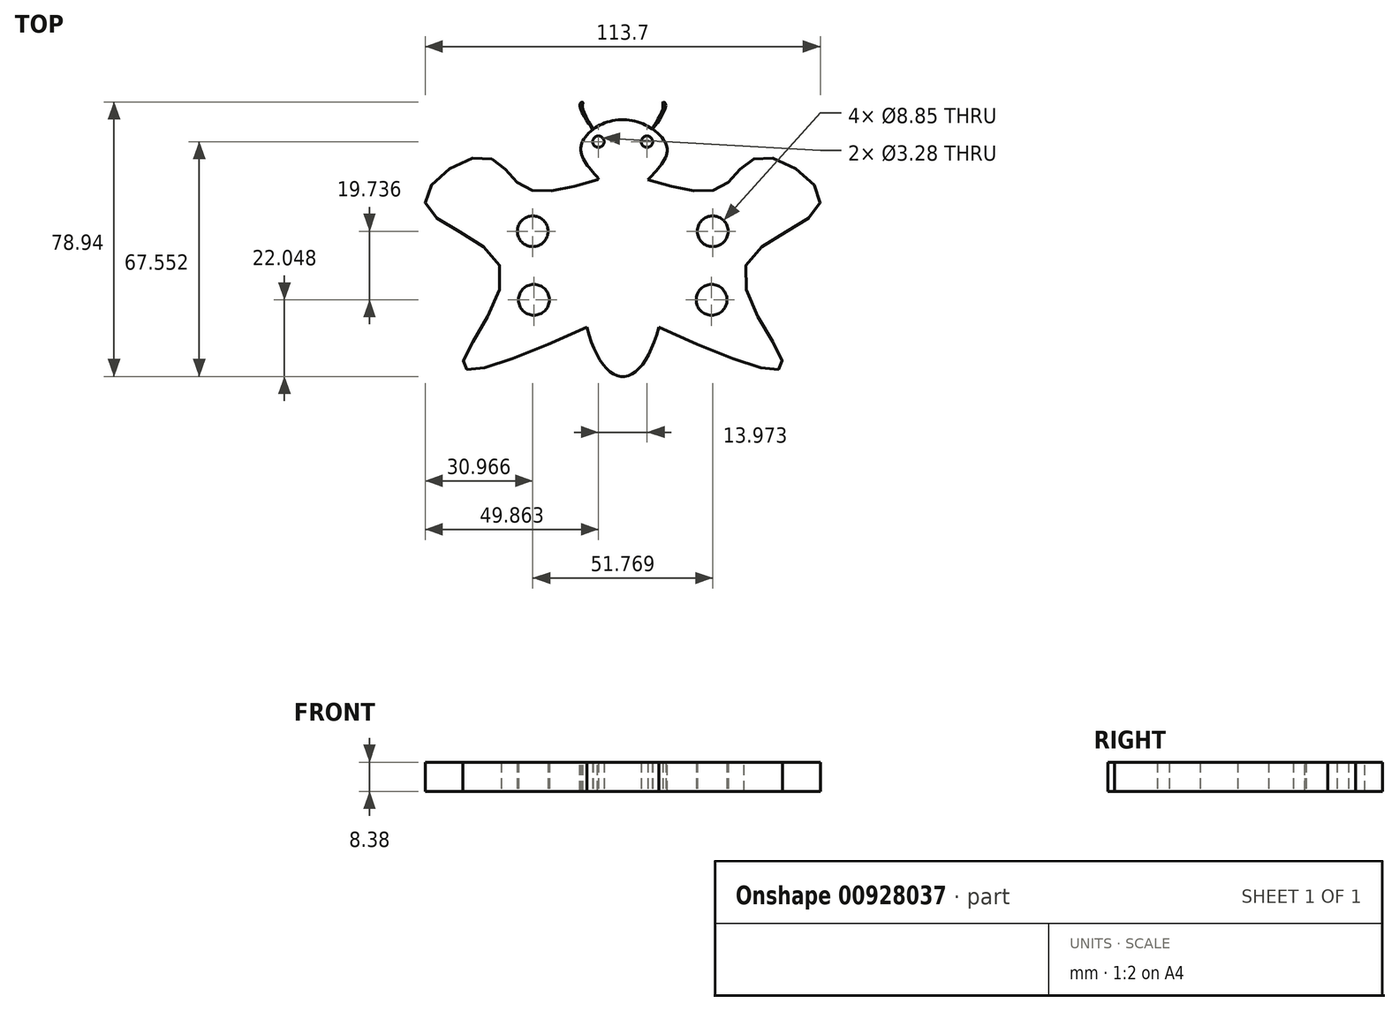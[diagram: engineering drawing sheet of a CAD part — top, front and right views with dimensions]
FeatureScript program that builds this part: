
annotation { "Feature Type Name" : "Feature", "Feature Type Description" : "" }
export const myFeature = defineFeature(function(context is Context, id is Id, definition is map)
    precondition{}
    {
        {
            var Q0;
            Q0=qCreatedBy(makeId("Top.planeOp"),FACE);
            var sketch = newSketch(context, id + "F0", { "sketchPlane" : qUnion([Q0])});
            skEllipse(sketch, "E0", {"center": v(0, 0) * mm, "majorRadius": 31.25 * mm, "minorRadius": 12.36 * mm, "majorAxis": v(0, -1)});
            skFitSpline(sketch, "E1", {"points": [v(-6.99, 25.78) * mm, v(-11.98, 35.24) * mm, v(0, 42.68) * mm, v(12.68, 34.77) * mm, v(7.23, 25.35) * mm], "startDerivative": vector(-36.9, 40.54) * mm, "endDerivative": vector(-38.54, -39.6) * mm});
            skCircle(sketch, "E2", {"center": v(-6.99, 36.3) * mm, "radius": 1.64 * mm});
            skCircle(sketch, "E3.MirrorC", {"center": v(6.99, 36.3) * mm, "radius": 1.64 * mm});
            skFitSpline(sketch, "E4", {"points": [v(7.23, 25.35) * mm, v(28.57, 23.33) * mm, v(39.9, 31.9) * mm, v(56.78, 18.63) * mm, v(35.2, 0) * mm, v(46, -27.84) * mm, v(10.34, -17.1) * mm], "startDerivative": vector(158.4, -47.63) * mm, "endDerivative": vector(-259.87, 114.92) * mm});
            skFitSpline(sketch, "E5.MirrorCS", {"points": [v(-7.23, 25.35) * mm, v(-28.57, 23.33) * mm, v(-39.9, 31.9) * mm, v(-56.78, 18.63) * mm, v(-35.2, 0) * mm, v(-46, -27.84) * mm, v(-10.34, -17.1) * mm], "startDerivative": vector(-158.4, -47.63) * mm, "endDerivative": vector(259.87, 114.92) * mm});
            skFitSpline(sketch, "E6", {"points": [v(-8.51, 39.87) * mm, v(-12.37, 46.84) * mm, v(-11.54, 47.67) * mm, v(-11.54, 46.01) * mm, v(-8.51, 39.87) * mm]});
            skFitSpline(sketch, "E7.MirrorC", {"points": [v(8.51, 39.87) * mm, v(12.37, 46.84) * mm, v(11.54, 47.67) * mm, v(11.54, 46.01) * mm, v(8.51, 39.87) * mm]});
            skCircle(sketch, "E8", {"center": v(-25.88, 10.53) * mm, "radius": 4.43 * mm});
            skCircle(sketch, "E9", {"center": v(-25.56, -9.2) * mm, "radius": 4.43 * mm});
            skCircle(sketch, "E10.MirrorC", {"center": v(25.88, 10.53) * mm, "radius": 4.43 * mm});
            skCircle(sketch, "E11.MirrorC", {"center": v(25.56, -9.2) * mm, "radius": 4.43 * mm});
            skSolve(sketch);
        }
        {
            var Q0;
            Q0 = qSketchRegion(id + "F0", true);
            extrude(context, id + "F1", {"entities" : qUnion([Q0]), "depth" : 8.38 * mm, "offsetDistance" : 25.4 * mm});
        }
    });
